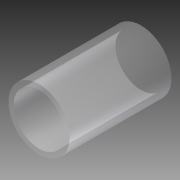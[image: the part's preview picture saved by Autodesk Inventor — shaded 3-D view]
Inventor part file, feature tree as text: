
AUTODESK INVENTOR PART (.ipt)
format: ipt  version: 2015 (Build 190159000, 159)  size: 84,480 bytes
history: native  units: mm
features: extrude x1, sketch x1
ambient origin geometry x8: Origin, YZ Plane, XZ Plane, XY Plane, X Axis, Y Axis, Z Axis, Center Point
bodies: Solid1 (feature_tree)
feature tree (2):
  extrude  "Extrusion1"  Depth=200.0mm
  sketch  "Sketch1"  dims[d0=120.0mm d1=100.0mm d2=200.0mm d3=0.0mm]
